# Revit family: РИДАН_RJIP Premium FB_WW_WG DN50-600
name_source: partatom
category: Арматура трубопроводов
units: mm (PartAtom-declared; Revit-internal decimal feet)

## family parameters
Всегда вертикально = Да
На основе рабочей плоскости = Нет
Общий = Нет
При загрузке вырезать с полостями = Нет
Размер круглого соединителя = Использовать диаметр
Тип детали = Вставляется

## types (13) — shared parameters
ADSK_Версия Revit = 2019
ADSK_Версия семейства = 1.0
ADSK_Единица измерения = шт.
ADSK_Завод-изготовитель = ООО «Ридан-Трейд»
ADSK_Количество = 1
ADSK_Потеря давления жидкости = 0.0 Па
ADSK_Расход жидкости = 0 м³/ч
LT = Table
URL = https://ridan.ru
Изготовитель = ООО «Ридан-Трейд»

## per-type parameters (varying)
- DN 50: ADSK_Диаметр условный=50 мм; ADSK_Код изделия=065N1123R; ADSK_Марка=RJIP Premium FB/WW/WG DN50; ADSK_Масса=9.6; ADSK_Наименование=RJIP Premium Кран шаровой FB WW DN50 PN25 WG; ADSK_Пропускная способность=189 м³/ч; Bot=Нет; a=44 мм; b=46 мм; c=120 мм; d=60 мм; e=101 мм; f=93 мм; g=114 мм; h=60 мм; i=90 мм; j=34 мм; k=70 мм; l=20 мм; m=300 мм; Редуктор DN125-150=Нет; Редуктор DN200=Нет; Редуктор DN250-300=Нет; Редуктор DN350-400=Нет; Редуктор DN500=Нет; Редуктор DN50_65=Да; Редуктор DN600=Нет; Редуктор DN80-100=Нет
- DN 65: ADSK_Диаметр условный=65 мм; ADSK_Код изделия=065N1131R; ADSK_Марка=RJIP Premium FB/WW/WG DN65; ADSK_Масса=12.6; ADSK_Наименование=RJIP Premium Кран шаровой FB WW DN65 PN25 WG; ADSK_Пропускная способность=328 м³/ч; Bot=Нет; a=39 мм; b=36 мм; c=150 мм; d=75 мм; e=117 мм; f=109 мм; g=140 мм; h=76 мм; i=90 мм; j=39 мм; k=80 мм; l=20 мм; m=300 мм; Редуктор DN125-150=Нет; Редуктор DN200=Нет; Редуктор DN250-300=Нет; Редуктор DN350-400=Нет; Редуктор DN500=Нет; Редуктор DN50_65=Нет; Редуктор DN600=Нет; Редуктор DN80-100=Да
- DN 80: ADSK_Диаметр условный=80 мм; ADSK_Код изделия=065N1136R; ADSK_Марка=RJIP Premium FB/WW/WG DN80; ADSK_Масса=15.6; ADSK_Наименование=RJIP Premium Кран шаровой FB WW DN80 PN25 WG; ADSK_Пропускная способность=494 м³/ч; Bot=Нет; a=33 мм; b=50 мм; c=160 мм; d=80 мм; e=129 мм; f=121 мм; g=159 мм; h=89 мм; i=90 мм; j=39 мм; k=96 мм; l=20 мм; m=325 мм; Редуктор DN125-150=Нет; Редуктор DN200=Нет; Редуктор DN250-300=Нет; Редуктор DN350-400=Нет; Редуктор DN500=Нет; Редуктор DN50_65=Нет; Редуктор DN600=Нет; Редуктор DN80-100=Да
- DN 100: ADSK_Диаметр условный=100 мм; ADSK_Код изделия=065N1141R; ADSK_Марка=RJIP Premium FB/WW/WG DN100; ADSK_Масса=22.6; ADSK_Наименование=RJIP Premium Кран шаровой FB WW DN100 PN25 WG; ADSK_Пропускная способность=1358 м³/ч; Bot=Нет; a=25 мм; b=44 мм; c=183 мм; d=92 мм; e=142 мм; f=129 мм; g=180 мм; h=108 мм; i=125 мм; j=49 мм; k=113 мм; l=20 мм; m=320 мм; Редуктор DN125-150=Да; Редуктор DN200=Нет; Редуктор DN250-300=Нет; Редуктор DN350-400=Нет; Редуктор DN500=Нет; Редуктор DN50_65=Нет; Редуктор DN600=Нет; Редуктор DN80-100=Нет
- DN 125: ADSK_Диаметр условный=125 мм; ADSK_Код изделия=065N1146R; ADSK_Марка=RJIP Premium FB/WW/WG DN125; ADSK_Масса=31.2; ADSK_Наименование=RJIP Premium Кран шаровой FB WW DN125 PN25 WG; ADSK_Пропускная способность=2156 м³/ч; Bot=Нет; a=36 мм; b=29 мм; c=220 мм; d=110 мм; e=162 мм; f=149 мм; g=219 мм; h=133 мм; i=125 мм; j=49 мм; k=129 мм; l=20 мм; m=350 мм; Редуктор DN125-150=Да; Редуктор DN200=Нет; Редуктор DN250-300=Нет; Редуктор DN350-400=Нет; Редуктор DN500=Нет; Редуктор DN50_65=Нет; Редуктор DN600=Нет; Редуктор DN80-100=Нет
- DN 150: ADSK_Диаметр условный=150 мм; ADSK_Код изделия=065N1151R; ADSK_Марка=RJIP Premium FB/WW/WG DN150; ADSK_Масса=60; ADSK_Наименование=RJIP Premium Кран шаровой FB WW DN150 PN25 WG; ADSK_Пропускная способность=2372 м³/ч; Bot=Да; a=13 мм; b=92 мм; c=270 мм; d=135 мм; e=215 мм; f=197 мм; g=273 мм; h=159 мм; i=150 мм; j=78 мм; k=185 мм; l=48 мм; m=480 мм; Редуктор DN125-150=Нет; Редуктор DN200=Да; Редуктор DN250-300=Нет; Редуктор DN350-400=Нет; Редуктор DN500=Нет; Редуктор DN50_65=Нет; Редуктор DN600=Нет; Редуктор DN80-100=Нет
- DN 200: ADSK_Диаметр условный=200 мм; ADSK_Код изделия=065N1156R; ADSK_Марка=RJIP Premium FB/WW/WG DN200; ADSK_Масса=110; ADSK_Наименование=RJIP Premium Кран шаровой FB WW DN200 PN25 WG; ADSK_Пропускная способность=3698 м³/ч; Bot=Да; a=47 мм; b=56 мм; c=390 мм; d=195 мм; e=254 мм; f=236 мм; g=351 мм; h=219 мм; i=210 мм; j=78 мм; k=224 мм; l=48 мм; m=595 мм; Редуктор DN125-150=Нет; Редуктор DN200=Нет; Редуктор DN250-300=Да; Редуктор DN350-400=Нет; Редуктор DN500=Нет; Редуктор DN50_65=Нет; Редуктор DN600=Нет; Редуктор DN80-100=Нет
- DN 250: ADSK_Диаметр условный=250 мм; ADSK_Код изделия=065N1161R; ADSK_Марка=RJIP Premium FB/WW/WG DN250; ADSK_Масса=170; ADSK_Наименование=RJIP Premium Кран шаровой FB WW DN250 PN25 WG; ADSK_Пропускная способность=5725 м³/ч; Bot=Да; a=50 мм; b=43 мм; c=500 мм; d=250 мм; e=302 мм; f=284 мм; g=426 мм; h=273 мм; i=210 мм; j=88 мм; k=278 мм; l=62 мм; m=685 мм; Редуктор DN125-150=Нет; Редуктор DN200=Нет; Редуктор DN250-300=Да; Редуктор DN350-400=Нет; Редуктор DN500=Нет; Редуктор DN50_65=Нет; Редуктор DN600=Нет; Редуктор DN80-100=Нет
- DN 300: ADSK_Диаметр условный=300 мм; ADSK_Код изделия=065N1166R; ADSK_Марка=RJIP Premium FB/WW/WG DN300; ADSK_Масса=329; ADSK_Наименование=RJIP Premium Кран шаровой FB WW DN300 PN25 WG; ADSK_Пропускная способность=22560 м³/ч; Bot=Да; a=125 мм; b=63 мм; c=387 мм; d=193 мм; e=347 мм; f=329 мм; g=505 мм; h=325 мм; i=210 мм; j=98 мм; k=340 мм; l=100 мм; m=762 мм; Редуктор DN125-150=Нет; Редуктор DN200=Нет; Редуктор DN250-300=Нет; Редуктор DN350-400=Да; Редуктор DN500=Нет; Редуктор DN50_65=Нет; Редуктор DN600=Нет; Редуктор DN80-100=Нет
- DN 350: ADSK_Диаметр условный=350 мм; ADSK_Код изделия=065N1173R; ADSK_Марка=RJIP Premium FB/WW/WG DN350; ADSK_Масса=423; ADSK_Наименование=RJIP Premium Кран шаровой FB WW DN350 PN25 WG; ADSK_Пропускная способность=27680 м³/ч; Bot=Да; a=131 мм; b=76 мм; c=425 мм; d=212 мм; e=383 мм; f=365 мм; g=556 мм; h=377 мм; i=210 мм; j=124 мм; k=365 мм; l=100 мм; m=838 мм; Редуктор DN125-150=Нет; Редуктор DN200=Нет; Редуктор DN250-300=Нет; Редуктор DN350-400=Да; Редуктор DN500=Нет; Редуктор DN50_65=Нет; Редуктор DN600=Нет; Редуктор DN80-100=Нет
- DN 400: ADSK_Диаметр условный=400 мм; ADSK_Код изделия=065N1176R; ADSK_Марка=RJIP Premium FB/WW/WG DN400; ADSK_Масса=428; ADSK_Наименование=RJIP Premium Кран шаровой FB WW DN400 PN25 WG; ADSK_Пропускная способность=35050 м³/ч; Bot=Да; a=117 мм; b=91 мм; c=497 мм; d=249 мм; e=446 мм; f=421 мм; g=676 мм; h=426 мм; i=300 мм; j=150 мм; k=462 мм; l=125 мм; m=915 мм; Редуктор DN125-150=Нет; Редуктор DN200=Нет; Редуктор DN250-300=Нет; Редуктор DN350-400=Нет; Редуктор DN500=Да; Редуктор DN50_65=Нет; Редуктор DN600=Нет; Редуктор DN80-100=Нет
- DN 500: ADSK_Диаметр условный=500 мм; ADSK_Код изделия=065N1183R; ADSK_Марка=RJIP Premium FB/WW/WG DN500; ADSK_Масса=1176; ADSK_Наименование=RJIP Premium Кран шаровой FB WW DN500 PN25 WG; ADSK_Пропускная способность=55005 м³/ч; Bot=Да; a=168 мм; b=109 мм; c=589 мм; d=295 мм; e=529 мм; f=501 мм; g=808 мм; h=530 мм; i=350 мм; j=165 мм; k=490 мм; l=125 мм; m=1143 мм; Редуктор DN125-150=Нет; Редуктор DN200=Нет; Редуктор DN250-300=Нет; Редуктор DN350-400=Нет; Редуктор DN500=Нет; Редуктор DN50_65=Нет; Редуктор DN600=Да; Редуктор DN80-100=Нет
- DN 600: ADSK_Диаметр условный=600 мм; ADSK_Код изделия=065N1186R; ADSK_Марка=RJIP Premium FB/WW/WG DN600; ADSK_Масса=2018; ADSK_Наименование=RJIP Premium Кран шаровой FB WW DN600 PN25 WG; ADSK_Пропускная способность=91500 м³/ч; Bot=Да; a=263 мм; b=90 мм; c=675 мм; d=337 мм; e=623 мм; f=595 мм; g=1012 мм; h=630 мм; i=350 мм; j=177 мм; k=629 мм; l=138 мм; m=1380 мм; Редуктор DN125-150=Нет; Редуктор DN200=Нет; Редуктор DN250-300=Нет; Редуктор DN350-400=Нет; Редуктор DN500=Нет; Редуктор DN50_65=Нет; Редуктор DN600=Да; Редуктор DN80-100=Нет
